# Revit family: Legrand XL³-S 630 24 Modules à la rangée
name_source: partatom
category: Equipement électrique
units: mm (PartAtom-declared; Revit-internal decimal feet)

## family parameters
Basée sur le plan de construction = Non
Configuration du panneau = Deux colonnes, circuits au sein
Cote de connecteur circulaire = Utiliser le diamètre
Couper avec des vides une fois chargée = Non
Numéro OmniClass = 23.80.30.11.17
Partagée = Non
Point de calcul de pièce = Non
Titre OmniClass = Distribution Boards and Control Panels
Toujours verticalement = Oui
Type d'élément = Tableau de raccordement

## types (11) — shared parameters
Conditions Générale d'Utilisation = https://export.legrand.com
ETIM Class 6.0 = EC000261
Fabricant = Legrand
Hauteur Base = 100 mm  [stored 0.328084 ft]
IK = 08
IP = 40
Image du type = XL3S_630_24M_337582_p_230130.jpg
Largeur = 604 mm  [stored 1.98163 ft]
Largeur zone d'installation = 1102 mm  [stored 3.61549 ft]
Matière = Acier
RAL = 9003
URL = www.legrand.fr
distance avant zone d'installation = 604 mm  [stored 1.98163 ft]
distance coté zone d'installation = 249 mm  [stored 0.816929 ft]
kit finition = Non
kit finition 337960_337973 = Non
kit finition 337961_337973 = Non
kit finition 337962_337973 = Non
kit finition 337963_337973 = Non
kit finition 337964_337973 = Non
kit finition 337965_337973 = Non
kit finition 337966_337973 = Non
kit finition 337967_337973 = Non
kit finition 337968_337973 = Non
kit finition 337969_337973 = Non
kit finition 337970_337973 = Non
panneau latéral droit = Oui
panneau latéral gauche = Oui
porte = Oui
profondeur = 249 mm  [stored 0.816929 ft]
profondeur zone d'installation = 853 mm  [stored 2.79856 ft]
socle = Oui
zero-valued in all types: Elévation par défaut

## per-type parameters (varying)
- Enveloppe de distribution - XL³ S 630 - Coffret plastronnable - Métal - hauteur 750 - 24 modules: Description=Ref 337522 - Enveloppe de distribution - XL³ S 630 - Coffret plastronnable - Métal - hauteur 750 - 24 modules; Hauteur=924 mm  [stored 3.0315 ft]; enveloppe 337522=Oui; enveloppe 337532=Non; enveloppe 337542=Non; enveloppe 337552=Non; enveloppe 337562=Non; enveloppe 337572=Non; enveloppe 337582=Non; enveloppe 337592=Non; enveloppe 337602=Non; enveloppe 337612=Non; enveloppe 337622=Non; panneau latéral droit 337862=Oui; panneau latéral droit 337863=Non; panneau latéral droit 337864=Non; panneau latéral droit 337865=Non; panneau latéral droit 337866=Non; panneau latéral droit 337867=Non; panneau latéral droit 337868=Non; panneau latéral droit 337869=Non; panneau latéral droit 337870=Non; panneau latéral droit 337871=Non; panneau latéral droit 337872=Non; panneau latéral gauche 337862=Oui; panneau latéral gauche 337863=Non; panneau latéral gauche 337864=Non; panneau latéral gauche 337865=Non; panneau latéral gauche 337866=Non; panneau latéral gauche 337867=Non; panneau latéral gauche 337868=Non; panneau latéral gauche 337869=Non; panneau latéral gauche 337870=Non; panneau latéral gauche 337871=Non; panneau latéral gauche 337872=Non; porte 337642=Oui; porte 337652=Non; porte 337662=Non; porte 337672=Non; porte 337682=Non; porte 337692=Non; porte 337702=Non; porte 337712=Non; porte 337722=Non; porte 337732=Non; porte 337742=Non
- Enveloppe de distribution - XL³ S 630 - Coffret plastronnable - Métal - hauteur 900 - 24 modules: Description=Ref 337532 - Enveloppe de distribution - XL³ S 630 - Coffret plastronnable - Métal - hauteur 900 - 24 modules; Hauteur=1074 mm  [stored 3.52362 ft]; enveloppe 337522=Non; enveloppe 337532=Oui; enveloppe 337542=Non; enveloppe 337552=Non; enveloppe 337562=Non; enveloppe 337572=Non; enveloppe 337582=Non; enveloppe 337592=Non; enveloppe 337602=Non; enveloppe 337612=Non; enveloppe 337622=Non; panneau latéral droit 337862=Non; panneau latéral droit 337863=Oui; panneau latéral droit 337864=Non; panneau latéral droit 337865=Non; panneau latéral droit 337866=Non; panneau latéral droit 337867=Non; panneau latéral droit 337868=Non; panneau latéral droit 337869=Non; panneau latéral droit 337870=Non; panneau latéral droit 337871=Non; panneau latéral droit 337872=Non; panneau latéral gauche 337862=Non; panneau latéral gauche 337863=Oui; panneau latéral gauche 337864=Non; panneau latéral gauche 337865=Non; panneau latéral gauche 337866=Non; panneau latéral gauche 337867=Non; panneau latéral gauche 337868=Non; panneau latéral gauche 337869=Non; panneau latéral gauche 337870=Non; panneau latéral gauche 337871=Non; panneau latéral gauche 337872=Non; porte 337642=Non; porte 337652=Oui; porte 337662=Non; porte 337672=Non; porte 337682=Non; porte 337692=Non; porte 337702=Non; porte 337712=Non; porte 337722=Non; porte 337732=Non; porte 337742=Non
- Enveloppe de distribution - XL³ S 630 - Coffret plastronnable - Métal - hauteur 1050 - 24 modules: Description=Ref 337542 - Enveloppe de distribution - XL³ S 630 - Coffret plastronnable - Métal - hauteur 1050 - 24 modules; Hauteur=1224 mm  [stored 4.01575 ft]; enveloppe 337522=Non; enveloppe 337532=Non; enveloppe 337542=Oui; enveloppe 337552=Non; enveloppe 337562=Non; enveloppe 337572=Non; enveloppe 337582=Non; enveloppe 337592=Non; enveloppe 337602=Non; enveloppe 337612=Non; enveloppe 337622=Non; panneau latéral droit 337862=Non; panneau latéral droit 337863=Non; panneau latéral droit 337864=Oui; panneau latéral droit 337865=Non; panneau latéral droit 337866=Non; panneau latéral droit 337867=Non; panneau latéral droit 337868=Non; panneau latéral droit 337869=Non; panneau latéral droit 337870=Non; panneau latéral droit 337871=Non; panneau latéral droit 337872=Non; panneau latéral gauche 337862=Non; panneau latéral gauche 337863=Non; panneau latéral gauche 337864=Oui; panneau latéral gauche 337865=Non; panneau latéral gauche 337866=Non; panneau latéral gauche 337867=Non; panneau latéral gauche 337868=Non; panneau latéral gauche 337869=Non; panneau latéral gauche 337870=Non; panneau latéral gauche 337871=Non; panneau latéral gauche 337872=Non; porte 337642=Non; porte 337652=Non; porte 337662=Oui; porte 337672=Non; porte 337682=Non; porte 337692=Non; porte 337702=Non; porte 337712=Non; porte 337722=Non; porte 337732=Non; porte 337742=Non
- Enveloppe de distribution - XL³ S 630 - Coffret plastronnable - Métal - hauteur 1200 - 24 modules: Description=Ref 337552 - Enveloppe de distribution - XL³ S 630 - Coffret plastronnable - Métal - hauteur 1200 - 24 modules; Hauteur=1374 mm  [stored 4.50787 ft]; enveloppe 337522=Non; enveloppe 337532=Non; enveloppe 337542=Non; enveloppe 337552=Oui; enveloppe 337562=Non; enveloppe 337572=Non; enveloppe 337582=Non; enveloppe 337592=Non; enveloppe 337602=Non; enveloppe 337612=Non; enveloppe 337622=Non; panneau latéral droit 337862=Non; panneau latéral droit 337863=Non; panneau latéral droit 337864=Non; panneau latéral droit 337865=Oui; panneau latéral droit 337866=Non; panneau latéral droit 337867=Non; panneau latéral droit 337868=Non; panneau latéral droit 337869=Non; panneau latéral droit 337870=Non; panneau latéral droit 337871=Non; panneau latéral droit 337872=Non; panneau latéral gauche 337862=Non; panneau latéral gauche 337863=Non; panneau latéral gauche 337864=Non; panneau latéral gauche 337865=Oui; panneau latéral gauche 337866=Non; panneau latéral gauche 337867=Non; panneau latéral gauche 337868=Non; panneau latéral gauche 337869=Non; panneau latéral gauche 337870=Non; panneau latéral gauche 337871=Non; panneau latéral gauche 337872=Non; porte 337642=Non; porte 337652=Non; porte 337662=Non; porte 337672=Oui; porte 337682=Non; porte 337692=Non; porte 337702=Non; porte 337712=Non; porte 337722=Non; porte 337732=Non; porte 337742=Non
- Enveloppe de distribution - XL³ S 630 - Coffret plastronnable - Métal - hauteur 1350 - 24 modules: Description=Ref 337562 - Enveloppe de distribution - XL³ S 630 - Coffret plastronnable - Métal - hauteur 1350 - 24 modules; Hauteur=1524 mm  [stored 5 ft]; enveloppe 337522=Non; enveloppe 337532=Non; enveloppe 337542=Non; enveloppe 337552=Non; enveloppe 337562=Oui; enveloppe 337572=Non; enveloppe 337582=Non; enveloppe 337592=Non; enveloppe 337602=Non; enveloppe 337612=Non; enveloppe 337622=Non; panneau latéral droit 337862=Non; panneau latéral droit 337863=Non; panneau latéral droit 337864=Non; panneau latéral droit 337865=Non; panneau latéral droit 337866=Oui; panneau latéral droit 337867=Non; panneau latéral droit 337868=Non; panneau latéral droit 337869=Non; panneau latéral droit 337870=Non; panneau latéral droit 337871=Non; panneau latéral droit 337872=Non; panneau latéral gauche 337862=Non; panneau latéral gauche 337863=Non; panneau latéral gauche 337864=Non; panneau latéral gauche 337865=Non; panneau latéral gauche 337866=Oui; panneau latéral gauche 337867=Non; panneau latéral gauche 337868=Non; panneau latéral gauche 337869=Non; panneau latéral gauche 337870=Non; panneau latéral gauche 337871=Non; panneau latéral gauche 337872=Non; porte 337642=Non; porte 337652=Non; porte 337662=Non; porte 337672=Non; porte 337682=Oui; porte 337692=Non; porte 337702=Non; porte 337712=Non; porte 337722=Non; porte 337732=Non; porte 337742=Non
- Enveloppe de distribution - XL³ S 630 - Coffret plastronnable - Métal - hauteur 1500 - 24 modules: Description=Ref 337572 - Enveloppe de distribution - XL³ S 630 - Coffret plastronnable - Métal - hauteur 1500 - 24 modules; Hauteur=1674 mm  [stored 5.49213 ft]; enveloppe 337522=Non; enveloppe 337532=Non; enveloppe 337542=Non; enveloppe 337552=Non; enveloppe 337562=Non; enveloppe 337572=Oui; enveloppe 337582=Non; enveloppe 337592=Non; enveloppe 337602=Non; enveloppe 337612=Non; enveloppe 337622=Non; panneau latéral droit 337862=Non; panneau latéral droit 337863=Non; panneau latéral droit 337864=Non; panneau latéral droit 337865=Non; panneau latéral droit 337866=Non; panneau latéral droit 337867=Oui; panneau latéral droit 337868=Non; panneau latéral droit 337869=Non; panneau latéral droit 337870=Non; panneau latéral droit 337871=Non; panneau latéral droit 337872=Non; panneau latéral gauche 337862=Non; panneau latéral gauche 337863=Non; panneau latéral gauche 337864=Non; panneau latéral gauche 337865=Non; panneau latéral gauche 337866=Non; panneau latéral gauche 337867=Oui; panneau latéral gauche 337868=Non; panneau latéral gauche 337869=Non; panneau latéral gauche 337870=Non; panneau latéral gauche 337871=Non; panneau latéral gauche 337872=Non; porte 337642=Non; porte 337652=Non; porte 337662=Non; porte 337672=Non; porte 337682=Non; porte 337692=Oui; porte 337702=Non; porte 337712=Non; porte 337722=Non; porte 337732=Non; porte 337742=Non
- Enveloppe de distribution - XL³ S 630 - Coffret plastronnable - Métal - hauteur 1650 - 24 modules: Description=Ref 337582 - Enveloppe de distribution - XL³ S 630 - Coffret plastronnable - Métal - hauteur 1650 - 24 modules; Hauteur=1824 mm  [stored 5.98425 ft]; enveloppe 337522=Non; enveloppe 337532=Non; enveloppe 337542=Non; enveloppe 337552=Non; enveloppe 337562=Non; enveloppe 337572=Non; enveloppe 337582=Oui; enveloppe 337592=Non; enveloppe 337602=Non; enveloppe 337612=Non; enveloppe 337622=Non; panneau latéral droit 337862=Non; panneau latéral droit 337863=Non; panneau latéral droit 337864=Non; panneau latéral droit 337865=Non; panneau latéral droit 337866=Non; panneau latéral droit 337867=Non; panneau latéral droit 337868=Oui; panneau latéral droit 337869=Non; panneau latéral droit 337870=Non; panneau latéral droit 337871=Non; panneau latéral droit 337872=Non; panneau latéral gauche 337862=Non; panneau latéral gauche 337863=Non; panneau latéral gauche 337864=Non; panneau latéral gauche 337865=Non; panneau latéral gauche 337866=Non; panneau latéral gauche 337867=Non; panneau latéral gauche 337868=Oui; panneau latéral gauche 337869=Non; panneau latéral gauche 337870=Non; panneau latéral gauche 337871=Non; panneau latéral gauche 337872=Non; porte 337642=Non; porte 337652=Non; porte 337662=Non; porte 337672=Non; porte 337682=Non; porte 337692=Non; porte 337702=Oui; porte 337712=Non; porte 337722=Non; porte 337732=Non; porte 337742=Non
- Enveloppe de distribution - XL³ S 630 - Coffret plastronnable - Métal - hauteur 1800 - 24 modules: Description=Ref 337592 - Enveloppe de distribution - XL³ S 630 - Coffret plastronnable - Métal - hauteur 1800 - 24 modules; Hauteur=1974 mm  [stored 6.47638 ft]; enveloppe 337522=Non; enveloppe 337532=Non; enveloppe 337542=Non; enveloppe 337552=Non; enveloppe 337562=Non; enveloppe 337572=Non; enveloppe 337582=Non; enveloppe 337592=Oui; enveloppe 337602=Non; enveloppe 337612=Non; enveloppe 337622=Non; panneau latéral droit 337862=Non; panneau latéral droit 337863=Non; panneau latéral droit 337864=Non; panneau latéral droit 337865=Non; panneau latéral droit 337866=Non; panneau latéral droit 337867=Non; panneau latéral droit 337868=Non; panneau latéral droit 337869=Oui; panneau latéral droit 337870=Non; panneau latéral droit 337871=Non; panneau latéral droit 337872=Non; panneau latéral gauche 337862=Non; panneau latéral gauche 337863=Non; panneau latéral gauche 337864=Non; panneau latéral gauche 337865=Non; panneau latéral gauche 337866=Non; panneau latéral gauche 337867=Non; panneau latéral gauche 337868=Non; panneau latéral gauche 337869=Oui; panneau latéral gauche 337870=Non; panneau latéral gauche 337871=Non; panneau latéral gauche 337872=Non; porte 337642=Non; porte 337652=Non; porte 337662=Non; porte 337672=Non; porte 337682=Non; porte 337692=Non; porte 337702=Non; porte 337712=Oui; porte 337722=Non; porte 337732=Non; porte 337742=Non
- Enveloppe de distribution - XL³ S 630 - Coffret plastronnable - Métal - hauteur 1950 - 24 modules: Description=Ref 337602 - Enveloppe de distribution - XL³ S 630 - Coffret plastronnable - Métal - hauteur 1950 - 24 modules; Hauteur=2124 mm  [stored 6.9685 ft]; enveloppe 337522=Non; enveloppe 337532=Non; enveloppe 337542=Non; enveloppe 337552=Non; enveloppe 337562=Non; enveloppe 337572=Non; enveloppe 337582=Non; enveloppe 337592=Non; enveloppe 337602=Oui; enveloppe 337612=Non; enveloppe 337622=Non; panneau latéral droit 337862=Non; panneau latéral droit 337863=Non; panneau latéral droit 337864=Non; panneau latéral droit 337865=Non; panneau latéral droit 337866=Non; panneau latéral droit 337867=Non; panneau latéral droit 337868=Non; panneau latéral droit 337869=Non; panneau latéral droit 337870=Oui; panneau latéral droit 337871=Non; panneau latéral droit 337872=Non; panneau latéral gauche 337862=Non; panneau latéral gauche 337863=Non; panneau latéral gauche 337864=Non; panneau latéral gauche 337865=Non; panneau latéral gauche 337866=Non; panneau latéral gauche 337867=Non; panneau latéral gauche 337868=Non; panneau latéral gauche 337869=Non; panneau latéral gauche 337870=Oui; panneau latéral gauche 337871=Non; panneau latéral gauche 337872=Non; porte 337642=Non; porte 337652=Non; porte 337662=Non; porte 337672=Non; porte 337682=Non; porte 337692=Non; porte 337702=Non; porte 337712=Non; porte 337722=Oui; porte 337732=Non; porte 337742=Non
- Enveloppe de distribution - XL³ S 630 - Coffret plastronnable - Métal - hauteur 2100 - 24 modules: Description=Ref 337612 - Enveloppe de distribution - XL³ S 630 - Coffret plastronnable - Métal - hauteur 2100 - 24 modules; Hauteur=2274 mm  [stored 7.46063 ft]; enveloppe 337522=Non; enveloppe 337532=Non; enveloppe 337542=Non; enveloppe 337552=Non; enveloppe 337562=Non; enveloppe 337572=Non; enveloppe 337582=Non; enveloppe 337592=Non; enveloppe 337602=Non; enveloppe 337612=Oui; enveloppe 337622=Non; panneau latéral droit 337862=Non; panneau latéral droit 337863=Non; panneau latéral droit 337864=Non; panneau latéral droit 337865=Non; panneau latéral droit 337866=Non; panneau latéral droit 337867=Non; panneau latéral droit 337868=Non; panneau latéral droit 337869=Non; panneau latéral droit 337870=Non; panneau latéral droit 337871=Oui; panneau latéral droit 337872=Non; panneau latéral gauche 337862=Non; panneau latéral gauche 337863=Non; panneau latéral gauche 337864=Non; panneau latéral gauche 337865=Non; panneau latéral gauche 337866=Non; panneau latéral gauche 337867=Non; panneau latéral gauche 337868=Non; panneau latéral gauche 337869=Non; panneau latéral gauche 337870=Non; panneau latéral gauche 337871=Oui; panneau latéral gauche 337872=Non; porte 337642=Non; porte 337652=Non; porte 337662=Non; porte 337672=Non; porte 337682=Non; porte 337692=Non; porte 337702=Non; porte 337712=Non; porte 337722=Non; porte 337732=Oui; porte 337742=Non
- Enveloppe de distribution - XL³ S 630 - Coffret plastronnable - Métal - hauteur 2250 - 24 modules: Description=Ref 337622 - Enveloppe de distribution - XL³ S 630 - Coffret plastronnable - Métal - hauteur 2250 - 24 modules; Hauteur=2424 mm  [stored 7.95276 ft]; enveloppe 337522=Non; enveloppe 337532=Non; enveloppe 337542=Non; enveloppe 337552=Non; enveloppe 337562=Non; enveloppe 337572=Non; enveloppe 337582=Non; enveloppe 337592=Non; enveloppe 337602=Non; enveloppe 337612=Non; enveloppe 337622=Oui; panneau latéral droit 337862=Non; panneau latéral droit 337863=Non; panneau latéral droit 337864=Non; panneau latéral droit 337865=Non; panneau latéral droit 337866=Non; panneau latéral droit 337867=Non; panneau latéral droit 337868=Non; panneau latéral droit 337869=Non; panneau latéral droit 337870=Non; panneau latéral droit 337871=Non; panneau latéral droit 337872=Oui; panneau latéral gauche 337862=Non; panneau latéral gauche 337863=Non; panneau latéral gauche 337864=Non; panneau latéral gauche 337865=Non; panneau latéral gauche 337866=Non; panneau latéral gauche 337867=Non; panneau latéral gauche 337868=Non; panneau latéral gauche 337869=Non; panneau latéral gauche 337870=Non; panneau latéral gauche 337871=Non; panneau latéral gauche 337872=Oui; porte 337642=Non; porte 337652=Non; porte 337662=Non; porte 337672=Non; porte 337682=Non; porte 337692=Non; porte 337702=Non; porte 337712=Non; porte 337722=Non; porte 337732=Non; porte 337742=Oui

note: [stored X ft] marks values corroborated as IEEE doubles in the binary element streams (Revit-internal decimal feet)
